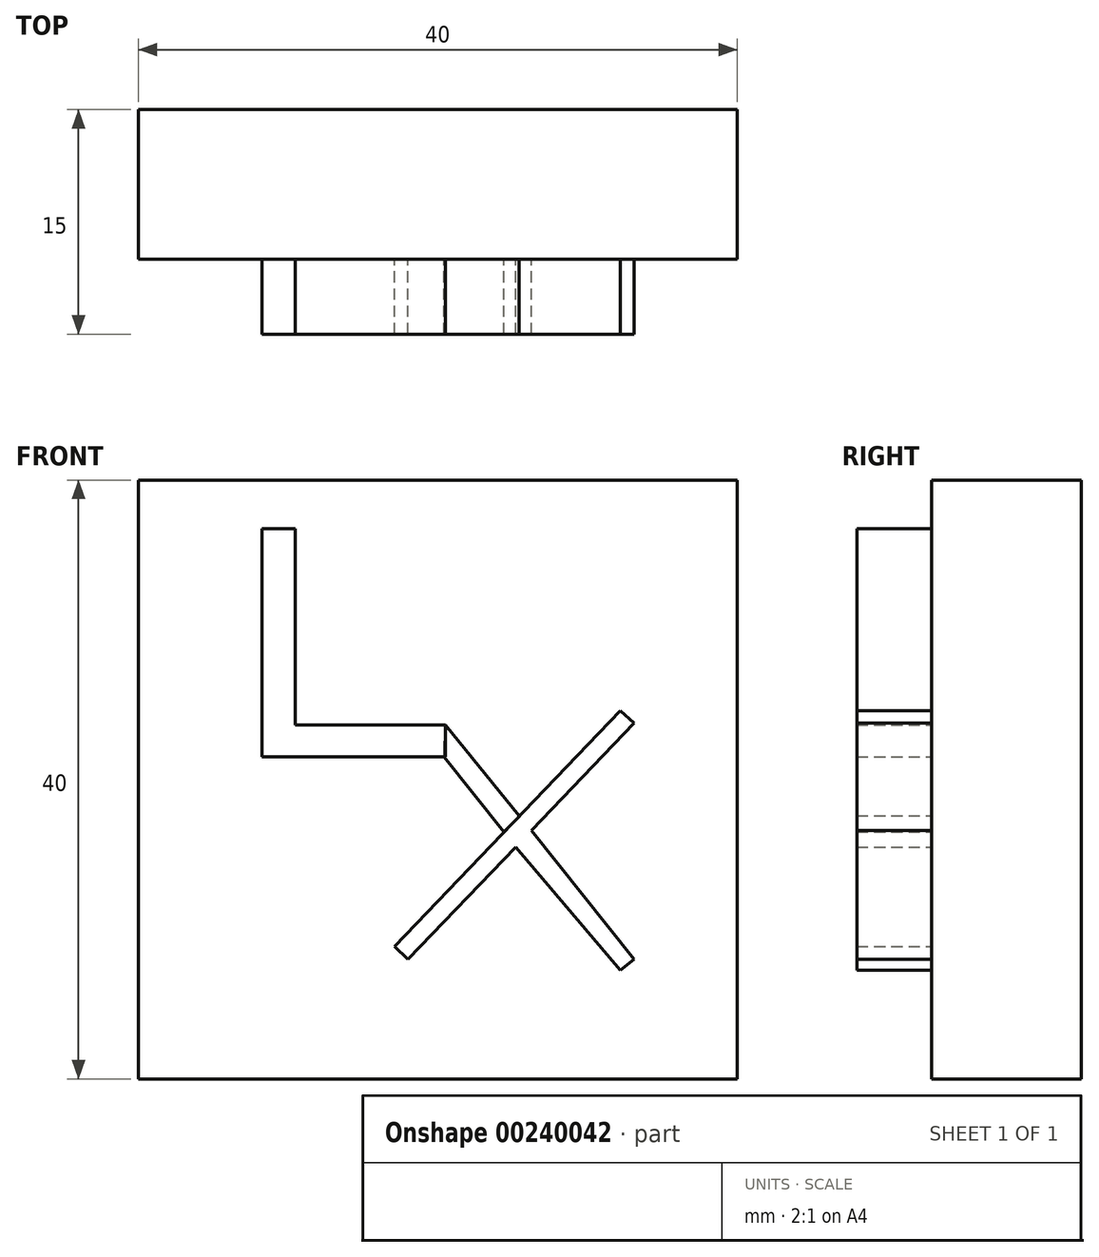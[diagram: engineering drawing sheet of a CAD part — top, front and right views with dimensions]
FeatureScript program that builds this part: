
annotation { "Feature Type Name" : "Feature", "Feature Type Description" : "" }
export const myFeature = defineFeature(function(context is Context, id is Id, definition is map)
    precondition{}
    {
        {
            var Q0;
            Q0=qCreatedBy(makeId("Front.planeOp"),FACE);
            var sketch = newSketch(context, id + "F0", { "sketchPlane" : qUnion([Q0])});
            skLineSegment(sketch, "E0", {"start": v(-40, 15.41) * mm, "end": v(-40, -24.59) * mm});
            skLineSegment(sketch, "E1", {"start": v(-40, 15.41) * mm, "end": v(0, 15.41) * mm});
            skLineSegment(sketch, "E2", {"start": v(-40, -24.59) * mm, "end": v(0, -24.59) * mm});
            skLineSegment(sketch, "E3", {"start": v(0, 15.41) * mm, "end": v(0, -24.59) * mm});
            skSolve(sketch);
        }
        {
            var Q0;
            Q0=makeQuery(id+"F0.imprint","IMPRINT",FACE,{"disambiguationData":[TD([[makeQuery(id+"F0.imprint","IMPRINT",EDGE,{"derivedFrom":sQuery(id+"F0.wireOp",EDGE,"E0")}),1.0]])]});
            extrude(context, id + "F1", {"entities" : qUnion([Q0]), "depth" : 10 * mm});
        }
        {
            var Q0;
            Q0=makeQuery(id+"F1.opExtrude","CAP_FACE",FACE,{"disambiguationData":[OSD([sQuery(id+"F0.wireOp",EDGE,"E0"),sQuery(id+"F0.wireOp",EDGE,"E1"),sQuery(id+"F0.wireOp",EDGE,"E2"),sQuery(id+"F0.wireOp",EDGE,"E3")])],"isStart":false});
            var sketch = newSketch(context, id + "F2", { "sketchPlane" : qUnion([Q0])});
            skLineSegment(sketch, "E4", {"start": v(-31.76, 12.17) * mm, "end": v(-31.76, -3.07) * mm});
            skLineSegment(sketch, "E5", {"start": v(-31.76, -3.07) * mm, "end": v(-19.5, -3.07) * mm});
            skLineSegment(sketch, "E6", {"start": v(-19.5, -3.07) * mm, "end": v(-19.5, -0.94) * mm});
            skLineSegment(sketch, "E7", {"start": v(-19.5, -0.94) * mm, "end": v(-29.52, -0.94) * mm});
            skLineSegment(sketch, "E8", {"start": v(-29.52, -0.94) * mm, "end": v(-29.52, 12.17) * mm});
            skLineSegment(sketch, "E9", {"start": v(-29.52, 12.17) * mm, "end": v(-31.76, 12.17) * mm});
            skSolve(sketch);
        }
        {
            var Q0;
            Q0=makeQuery(id+"F2.imprint","IMPRINT",FACE,{"disambiguationData":[TD([[makeQuery(id+"F2.imprint","IMPRINT",EDGE,{"derivedFrom":sQuery(id+"F2.wireOp",EDGE,"E4")}),-1.0]])]});
            var sketch = newSketch(context, id + "F3", { "sketchPlane" : qUnion([Q0])});
            skLineSegment(sketch, "E10", {"start": v(-19.5, -0.82) * mm, "end": v(-6.88, -16.6) * mm});
            skLineSegment(sketch, "E11", {"start": v(-6.88, -16.6) * mm, "end": v(-7.8, -17.34) * mm});
            skLineSegment(sketch, "E12", {"start": v(-7.8, -17.34) * mm, "end": v(-19.87, -3.13) * mm});
            skLineSegment(sketch, "E13", {"start": v(-6.88, -0.82) * mm, "end": v(-22, -16.6) * mm});
            skLineSegment(sketch, "E14", {"start": v(-22, -16.6) * mm, "end": v(-22.89, -15.74) * mm});
            skLineSegment(sketch, "E15", {"start": v(-22.89, -15.74) * mm, "end": v(-7.81, 0) * mm});
            skLineSegment(sketch, "E16", {"start": v(-7.81, 0) * mm, "end": v(-6.88, -0.82) * mm});
            skLineSegment(sketch, "E17", {"start": v(-19.5, -0.82) * mm, "end": v(-19.62, -0.92) * mm});
            skLineSegment(sketch, "E18", {"start": v(-19.62, -0.92) * mm, "end": v(-19.65, -0.94) * mm});
            skLineSegment(sketch, "E19", {"start": v(-19.87, -3.13) * mm, "end": v(-19.92, -3.07) * mm});
            skSolve(sketch);
        }
        {
            var Q0;
            Q0=makeQuery(id+"F2.imprint","IMPRINT",FACE,{"disambiguationData":[TD([[makeQuery(id+"F2.imprint","IMPRINT",EDGE,{"derivedFrom":sQuery(id+"F2.wireOp",EDGE,"E4")}),1.0]])]});
            extrude(context, id + "F4", {"entities" : qUnion([Q0]), "operationType" : NewBodyOperationType.ADD, "depth" : 5 * mm});
        }
        {
            var Q0;
            Q0 = qSketchRegion(id + "F3", true);
            extrude(context, id + "F5", {"entities" : qUnion([Q0]), "operationType" : NewBodyOperationType.ADD, "depth" : 5 * mm});
        }
        {
            var Q0;
            Q0=makeQuery(id+"F2.imprint","IMPRINT",FACE,{"disambiguationData":[TD([[makeQuery(id+"F2.imprint","IMPRINT",EDGE,{"derivedFrom":sQuery(id+"F2.wireOp",EDGE,"E4")}),-1.0]])]});
            var sketch = newSketch(context, id + "F6", { "sketchPlane" : qUnion([Q0])});
            skLineSegment(sketch, "E20", {"start": v(-14.57, -7) * mm, "end": v(-19.5, -0.93) * mm});
            skLineSegment(sketch, "E21", {"start": v(-15.58, -8.09) * mm, "end": v(-19.59, -3.08) * mm});
            skLineSegment(sketch, "E22", {"start": v(-19.59, -3.08) * mm, "end": v(-19.5, -3.08) * mm});
            skLineSegment(sketch, "E23", {"start": v(-19.5, -3.08) * mm, "end": v(-19.5, -0.93) * mm});
            skLineSegment(sketch, "E24", {"start": v(-15.58, -8.09) * mm, "end": v(-14.5, -7) * mm});
            skLineSegment(sketch, "E25", {"start": v(-14.5, -7) * mm, "end": v(-14.57, -7) * mm});
            skSolve(sketch);
        }
        {
            var Q0;
            Q0 = qSketchRegion(id + "F6", true);
            extrude(context, id + "F7", {"entities" : qUnion([Q0]), "depth" : 5 * mm});
        }
    });
